# Revit family: UNB_Specchio_Multiproduct_BIM_IT_T3350;T3351;T3352;T3353_NEW
name_source: partatom
category: Plumbing Fixtures
revit_build: Autodesk Revit 2017 (Build: 20160225_1515(x64)
units: mm (PartAtom-declared; Revit-internal decimal feet)

## family parameters
Cut with Voids When Loaded = No
Host = Face
Part Type = Normal
Room Calculation Point = No
Round Connector Dimension = Use Diameter
Shared = No

## types (4) — shared parameters
Accessori = http://www.idealstandard.it
AltezzaNominale = 700 mm  [stored 2.29659 ft]
Autore = Ideal Standard
Brand = Ideal Standard
CodiceDiPrestazione = EN
Colore = specchio
Connessione = piombatura
Default Elevation = 1500 mm  [stored 4.92126 ft]
DescrizioneClassifcazioneUni2015 = Bathroom furniture
Finitura = specchio
Forma = rettangolare
Garanzia = garanzia del produttore
IfcEsportaCome = BATHROOM FURNITURE
InformazioniDiProdotto = http://www.idealstandard.it
InstruzioniInstallazione = http://www.idealstandard.it
LunghezzaNominale = 26 mm
Materiale = bicchiere
PartiDiRicambio = http://www.idealstandard.it
ProfonditàNominale = 26 mm
Revisione = 1
RiferimentoClassificazioneUni2015 = MIRRORS
Spazio = interno
Telefono = 800 652 290
TipoDiDato = Fisso
TipoEspotazioneIfc = IfcFurnitureType
TipologiaVaso = Altro
URL = http://www.idealstandard.it
UnitàDurata = anno
UnitàDurataGaranzia = anno
UnitàLineare = millimetro
UnitàMonetaria = €
UnitàSuperficie = millimetro
UnitàVolume = litro
Versione = 1
VersioneClassificazioneUni2015 = IfcFurnitureType
zero-valued in all types: Cost, CostoDiSostituzione

## per-type parameters (varying)
| type | Caratteristiche | CodiceABarre | Description | LarghezzaNominale | Model | ModelloDiRiferimento | Nome | NomeOggettoBim | NumeroDiModello | PesoNetto | Riferimento |
| T3350 - 600 x 700 mirror | SPECCHIO HIGH AMBIENT 60X70 36,2W 230W | 8014140447429 | SPECCHIO HIGH AMBIENT 60X70 36,2W 230W | 600 mm | T3350BH | SPECCHIO HIGH AMBIENT 60X70 36,2W 230W | ISI_IdealStandard_Specchio_T3350 | ISI_IdealStandard_Specchio_T3350 | T3350BH | 6.12 Kg | T3350 |
| T3351 - 800 x 700 mirror | SPECCHIO HIGH AMBIENT 80X70 37,2W 230W | 8014140447436 | SPECCHIO HIGH AMBIENT 80X70 37,2W 230W | 800 mm  [stored 2.62467 ft] | T3351BH | SPECCHIO HIGH AMBIENT 80X70 37,2W 230W | ISI_IdealStandard_Specchio_T3351 | ISI_IdealStandard_Specchio_T3351 | T3351BH | 7.65 Kg | T3351 |
| T3352 - 1000 x 700 mirror | SPECCHIO HIGH AMBIENT 100X70 61,4W 230W | 8014140447443 | SPECCHIO HIGH AMBIENT 100X70 61,4W 230W | 1000 mm  [stored 3.28084 ft] | T3352BH | SPECCHIO HIGH AMBIENT 100X70 61,4W 230W | ISI_IdealStandard_Specchio_T3352 | ISI_IdealStandard_Specchio_T3352 | T3352BH | 9.42 Kg | T3352 |
| T3353 - 1200 x 700 mirror | SPECCHIO HIGH AMBIENT 120X70 63W 230W | 8014140447450 | SPECCHIO HIGH AMBIENT 120X70 63W 230W | 1200 mm | T3353BH | SPECCHIO HIGH AMBIENT 120X70 63W 230W | ISI_IdealStandard_Specchio_T3353 | ISI_IdealStandard_Specchio_T3353 | T3353BH | 11.00 Kg | T3353 |

note: [stored X ft] marks values corroborated as IEEE doubles in the binary element streams (Revit-internal decimal feet)

## geometry (parser evidence)
native form markers: Sweep x1
no freeform markers — native parametric forms only
